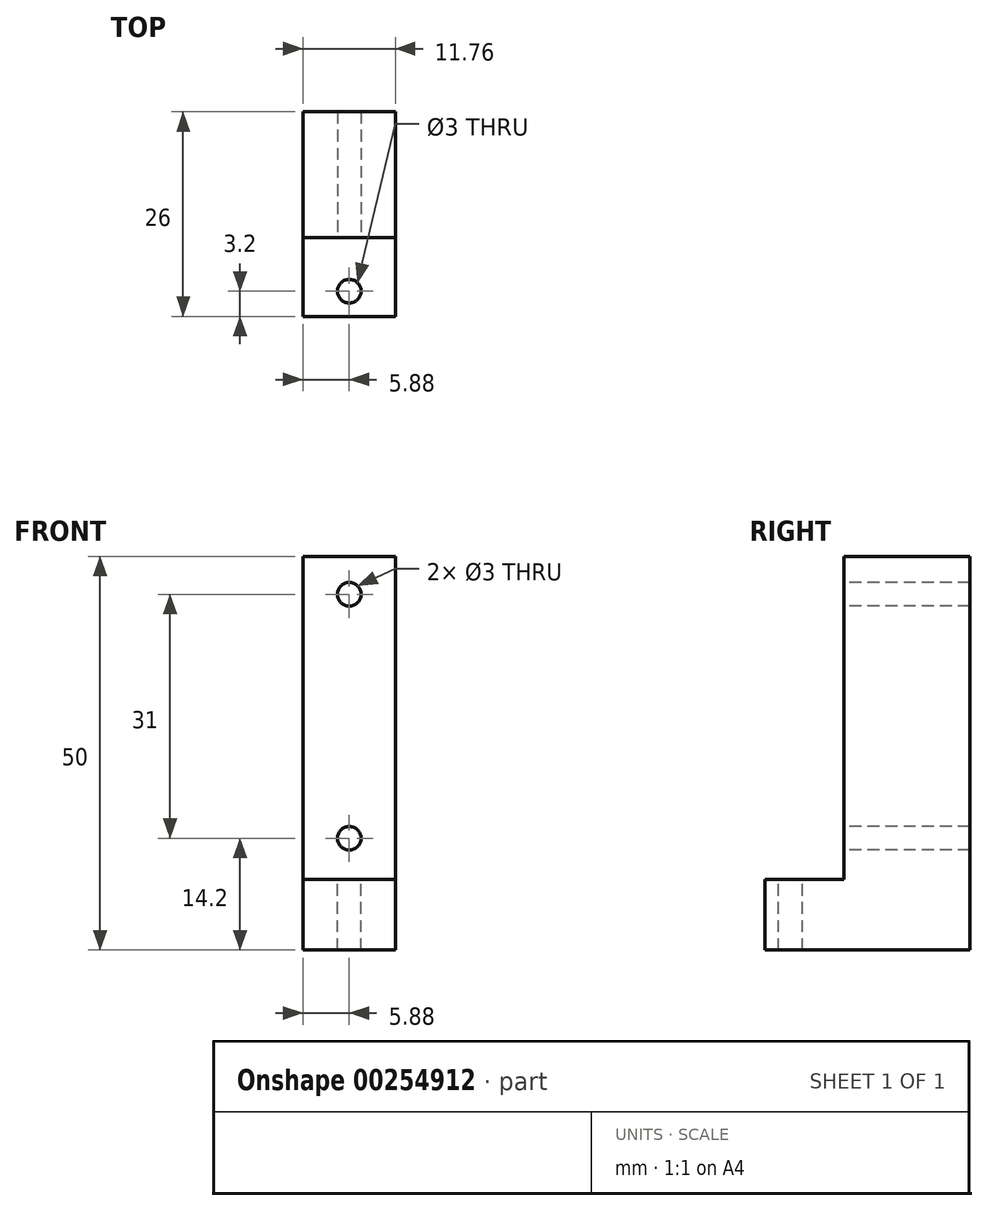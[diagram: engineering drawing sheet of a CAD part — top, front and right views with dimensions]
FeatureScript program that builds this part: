
annotation { "Feature Type Name" : "Feature", "Feature Type Description" : "" }
export const myFeature = defineFeature(function(context is Context, id is Id, definition is map)
    precondition{}
    {
        {
            var Q0;
            Q0=qCreatedBy(makeId("Front.planeOp"),FACE);
            var sketch = newSketch(context, id + "F0", { "sketchPlane" : qUnion([Q0])});
            skLineSegment(sketch, "E0.bottom", {"start": v(5.87, -25) * mm, "end": v(-5.88, -25) * mm});
            skLineSegment(sketch, "E0.top", {"start": v(5.88, 25) * mm, "end": v(-5.87, 25) * mm});
            skLineSegment(sketch, "E0.left", {"start": v(5.87, -25) * mm, "end": v(5.88, 25) * mm});
            skLineSegment(sketch, "E0.right", {"start": v(-5.88, -25) * mm, "end": v(-5.87, 25) * mm});
            skPoint(sketch, "E0.middle", {"position": v(0, 0) * mm});
            skSolve(sketch);
        }
        {
            var Q0;
            Q0 = qSketchRegion(id + "F0", true);
            extrude(context, id + "F1", {"entities" : qUnion([Q0]), "depth" : 16 * mm});
        }
        {
            var Q0;
            Q0=makeQuery(id+"F1.opExtrude","CAP_FACE",FACE,{"disambiguationData":[OSD([sQuery(id+"F0.wireOp",EDGE,"E0.bottom"),sQuery(id+"F0.wireOp",EDGE,"E0.top"),sQuery(id+"F0.wireOp",EDGE,"E0.left"),sQuery(id+"F0.wireOp",EDGE,"E0.right")])],"isStart":false});
            var sketch = newSketch(context, id + "F2", { "sketchPlane" : qUnion([Q0])});
            skCircle(sketch, "E1", {"center": v(0, 20.2) * mm, "radius": 1.5 * mm});
            skCircle(sketch, "E2", {"center": v(0, -10.8) * mm, "radius": 1.5 * mm});
            skSolve(sketch);
        }
        {
            var Q0;
            Q0 = qSketchRegion(id + "F2", true);
            extrude(context, id + "F3", {"entities" : qUnion([Q0]), "operationType" : NewBodyOperationType.REMOVE, "endBound" : BoundingType.THROUGH_ALL, "oppositeDirection" : true, "depth" : 25 * mm});
        }
        {
            var Q0;
            Q0=makeQuery(id+"F1.opExtrude","CAP_FACE",FACE,{"disambiguationData":[OSD([sQuery(id+"F0.wireOp",EDGE,"E0.bottom"),sQuery(id+"F0.wireOp",EDGE,"E0.top"),sQuery(id+"F0.wireOp",EDGE,"E0.left"),sQuery(id+"F0.wireOp",EDGE,"E0.right")])],"isStart":false});
            var sketch = newSketch(context, id + "F4", { "sketchPlane" : qUnion([Q0])});
            skLineSegment(sketch, "E3.bottom", {"start": v(-5.88, -16) * mm, "end": v(5.87, -16) * mm});
            skLineSegment(sketch, "E3.top", {"start": v(-5.88, -25) * mm, "end": v(5.87, -25) * mm});
            skLineSegment(sketch, "E3.left", {"start": v(-5.88, -16) * mm, "end": v(-5.88, -25) * mm});
            skLineSegment(sketch, "E3.right", {"start": v(5.87, -16) * mm, "end": v(5.87, -25) * mm});
            skSolve(sketch);
        }
        {
            var Q0;
            Q0 = qSketchRegion(id + "F4", true);
            extrude(context, id + "F5", {"entities" : qUnion([Q0]), "operationType" : NewBodyOperationType.ADD, "depth" : 10 * mm});
        }
        {
            var Q0;
            Q0=makeQuery(id+"F5.opExtrude","SWEPT_FACE",FACE,{"disambiguationData":[OSD([sQuery(id+"F4.wireOp",EDGE,"E3.bottom")])]});
            var sketch = newSketch(context, id + "F6", { "sketchPlane" : qUnion([Q0])});
            skCircle(sketch, "E4", {"center": v(0, -22.8) * mm, "radius": 1.5 * mm});
            skSolve(sketch);
        }
        {
            var Q0;
            Q0 = qSketchRegion(id + "F6", true);
            extrude(context, id + "F7", {"entities" : qUnion([Q0]), "operationType" : NewBodyOperationType.REMOVE, "endBound" : BoundingType.THROUGH_ALL, "oppositeDirection" : true, "depth" : 25 * mm});
        }
    });
